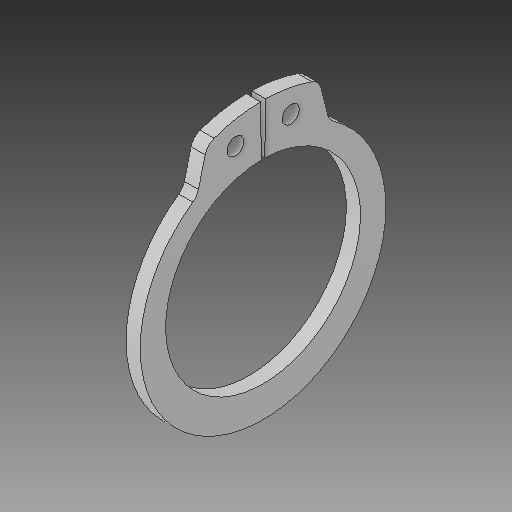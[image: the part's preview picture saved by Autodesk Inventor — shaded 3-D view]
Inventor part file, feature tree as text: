
AUTODESK INVENTOR PART (.ipt)
format: ipt  version: 2017 (Build 210142000, 142)  size: 110,592 bytes
history: native  units: in
note: dims shown in document units (in); Inventor stores cm internally (conversion verified against a paired STEP export)
features: fillet x1
ambient origin geometry x8: Origin, YZ Plane, XZ Plane, XY Plane, X Axis, Y Axis, Z Axis, Center Point
bodies: Solid1 (feature_tree)
feature tree (1):
  fillet  "Fillet1"  [1 undecoded]
note: 1 required parameter value undecoded (feature->parameter linkage not recoverable at this tier; creation-order binding heuristic only, values carry confidence <= 0.55)
